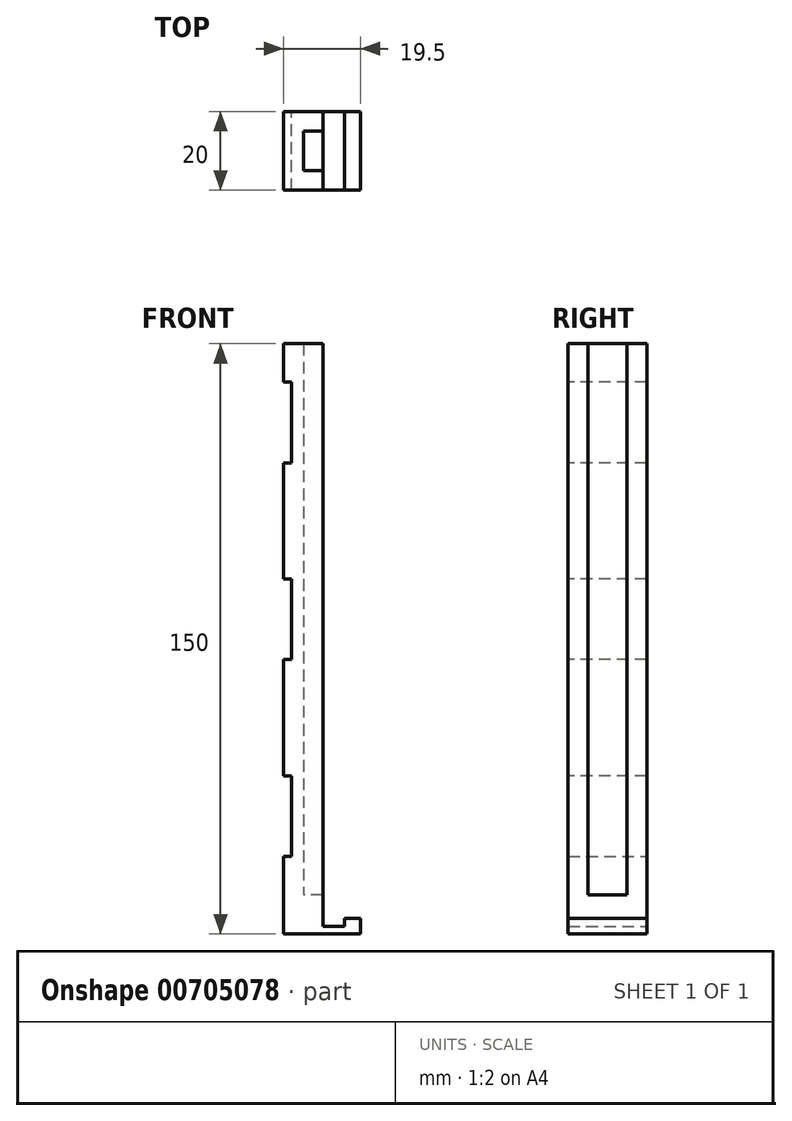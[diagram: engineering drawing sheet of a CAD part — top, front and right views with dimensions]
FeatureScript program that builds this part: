
annotation { "Feature Type Name" : "Feature", "Feature Type Description" : "" }
export const myFeature = defineFeature(function(context is Context, id is Id, definition is map)
    precondition{}
    {
        {
            var Q0;
            Q0=qCreatedBy(makeId("Top.planeOp"),FACE);
            var sketch = newSketch(context, id + "F0", { "sketchPlane" : qUnion([Q0])});
            skLineSegment(sketch, "E0.bottom", {"start": v(0, 0) * mm, "end": v(10, 0) * mm});
            skLineSegment(sketch, "E0.top", {"start": v(0, 20) * mm, "end": v(10, 20) * mm});
            skLineSegment(sketch, "E0.left", {"start": v(0, 0) * mm, "end": v(0, 20) * mm});
            skLineSegment(sketch, "E0.right", {"start": v(10, 0) * mm, "end": v(10, 20) * mm});
            skSolve(sketch);
        }
        {
            var Q0;
            Q0 = qSketchRegion(id + "F0", true);
            extrude(context, id + "F1", {"entities" : qUnion([Q0]), "depth" : 10 * mm, "offsetDistance" : 25 * mm});
        }
        {
            var Q0;
            Q0=qCreatedBy(makeId("Top.planeOp"),FACE);
            var sketch = newSketch(context, id + "F2", { "sketchPlane" : qUnion([Q0])});
            skLineSegment(sketch, "E1.bottom", {"start": v(10, 0) * mm, "end": v(15.5, 0) * mm});
            skLineSegment(sketch, "E1.top", {"start": v(10, 20) * mm, "end": v(15.5, 20) * mm});
            skLineSegment(sketch, "E1.left", {"start": v(10, 0) * mm, "end": v(10, 20) * mm});
            skLineSegment(sketch, "E1.right", {"start": v(15.5, 0) * mm, "end": v(15.5, 20) * mm});
            skSolve(sketch);
        }
        {
            var Q0;
            Q0 = qSketchRegion(id + "F2", true);
            extrude(context, id + "F3", {"entities" : qUnion([Q0]), "operationType" : NewBodyOperationType.ADD, "depth" : 2 * mm, "offsetDistance" : 25 * mm});
        }
        {
            var Q0;
            Q0=qCreatedBy(makeId("Top.planeOp"),FACE);
            var sketch = newSketch(context, id + "F4", { "sketchPlane" : qUnion([Q0])});
            skLineSegment(sketch, "E2.bottom", {"start": v(15.5, 20) * mm, "end": v(19.5, 20) * mm});
            skLineSegment(sketch, "E2.top", {"start": v(15.5, 0) * mm, "end": v(19.5, 0) * mm});
            skLineSegment(sketch, "E2.left", {"start": v(15.5, 20) * mm, "end": v(15.5, 0) * mm});
            skLineSegment(sketch, "E2.right", {"start": v(19.5, 20) * mm, "end": v(19.5, 0) * mm});
            skSolve(sketch);
        }
        {
            var Q0;
            Q0 = qSketchRegion(id + "F4", true);
            extrude(context, id + "F5", {"entities" : qUnion([Q0]), "operationType" : NewBodyOperationType.ADD, "depth" : 4 * mm, "offsetDistance" : 25 * mm});
        }
        {
            var Q0;
            Q0=makeQuery(id+"F1.opExtrude","CAP_FACE",FACE,{"disambiguationData":[OSD([sQuery(id+"F0.wireOp",EDGE,"E0.bottom"),sQuery(id+"F0.wireOp",EDGE,"E0.top"),sQuery(id+"F0.wireOp",EDGE,"E0.left"),sQuery(id+"F0.wireOp",EDGE,"E0.right")])],"isStart":false});
            var sketch = newSketch(context, id + "F6", { "sketchPlane" : qUnion([Q0])});
            skLineSegment(sketch, "E3.bottom", {"start": v(2, 20) * mm, "end": v(5, 20) * mm});
            skLineSegment(sketch, "E3.top", {"start": v(2, 0) * mm, "end": v(5, 0) * mm});
            skLineSegment(sketch, "E3.left", {"start": v(2, 20) * mm, "end": v(2, 0) * mm});
            skLineSegment(sketch, "E3.right", {"start": v(5, 20) * mm, "end": v(5, 0) * mm});
            skLineSegment(sketch, "E4.bottom", {"start": v(5, 20) * mm, "end": v(10, 20) * mm});
            skLineSegment(sketch, "E4.top", {"start": v(5, 15) * mm, "end": v(10, 15) * mm});
            skLineSegment(sketch, "E4.left", {"start": v(5, 20) * mm, "end": v(5, 15) * mm});
            skLineSegment(sketch, "E4.right", {"start": v(10, 20) * mm, "end": v(10, 15) * mm});
            skLineSegment(sketch, "E5.bottom", {"start": v(10, 0) * mm, "end": v(5, 0) * mm});
            skLineSegment(sketch, "E5.top", {"start": v(10, 5) * mm, "end": v(5, 5) * mm});
            skLineSegment(sketch, "E5.left", {"start": v(10, 0) * mm, "end": v(10, 5) * mm});
            skLineSegment(sketch, "E5.right", {"start": v(5, 0) * mm, "end": v(5, 5) * mm});
            skSolve(sketch);
        }
        {
            var Q0;
            Q0 = qSketchRegion(id + "F6", true);
            extrude(context, id + "F7", {"entities" : qUnion([Q0]), "operationType" : NewBodyOperationType.ADD, "depth" : 140 * mm, "offsetDistance" : 25 * mm});
        }
        {
            var Q0;
            Q0=makeQuery(id+"F7.opExtrude","SWEPT_FACE",FACE,{"disambiguationData":[OSD([sQuery(id+"F6.wireOp",EDGE,"E3.left")])]});
            var sketch = newSketch(context, id + "F8", { "sketchPlane" : qUnion([Q0])});
            skLineSegment(sketch, "E6.bottom", {"start": v(-20, 150) * mm, "end": v(0, 150) * mm});
            skLineSegment(sketch, "E6.top", {"start": v(-20, 140.25) * mm, "end": v(0, 140.25) * mm});
            skLineSegment(sketch, "E6.left", {"start": v(-20, 150) * mm, "end": v(-20, 140.25) * mm});
            skLineSegment(sketch, "E6.right", {"start": v(0, 150) * mm, "end": v(0, 140.25) * mm});
            skLineSegment(sketch, "E7.bottom", {"start": v(-20, 119.75) * mm, "end": v(0, 119.75) * mm});
            skLineSegment(sketch, "E7.top", {"start": v(-20, 90.25) * mm, "end": v(0, 90.25) * mm});
            skLineSegment(sketch, "E7.left", {"start": v(-20, 119.75) * mm, "end": v(-20, 90.25) * mm});
            skLineSegment(sketch, "E7.right", {"start": v(0, 119.75) * mm, "end": v(0, 90.25) * mm});
            skLineSegment(sketch, "E8.bottom", {"start": v(-20, 40.25) * mm, "end": v(0, 40.25) * mm});
            skLineSegment(sketch, "E8.top", {"start": v(-20, 69.75) * mm, "end": v(0, 69.75) * mm});
            skLineSegment(sketch, "E8.left", {"start": v(-20, 69.75) * mm, "end": v(-20, 40.25) * mm});
            skLineSegment(sketch, "E8.right", {"start": v(0, 69.75) * mm, "end": v(0, 40.25) * mm});
            skLineSegment(sketch, "E9.bottom", {"start": v(0, 10) * mm, "end": v(-20, 10) * mm});
            skLineSegment(sketch, "E9.top", {"start": v(0, 19.75) * mm, "end": v(-20, 19.75) * mm});
            skLineSegment(sketch, "E9.left", {"start": v(0, 10) * mm, "end": v(0, 19.75) * mm});
            skLineSegment(sketch, "E9.right", {"start": v(-20, 10) * mm, "end": v(-20, 19.75) * mm});
            skSolve(sketch);
        }
        {
            var Q0;
            Q0 = qSketchRegion(id + "F8", true);
            extrude(context, id + "F9", {"entities" : qUnion([Q0]), "operationType" : NewBodyOperationType.ADD, "depth" : 2 * mm, "offsetDistance" : 25 * mm});
        }
    });
